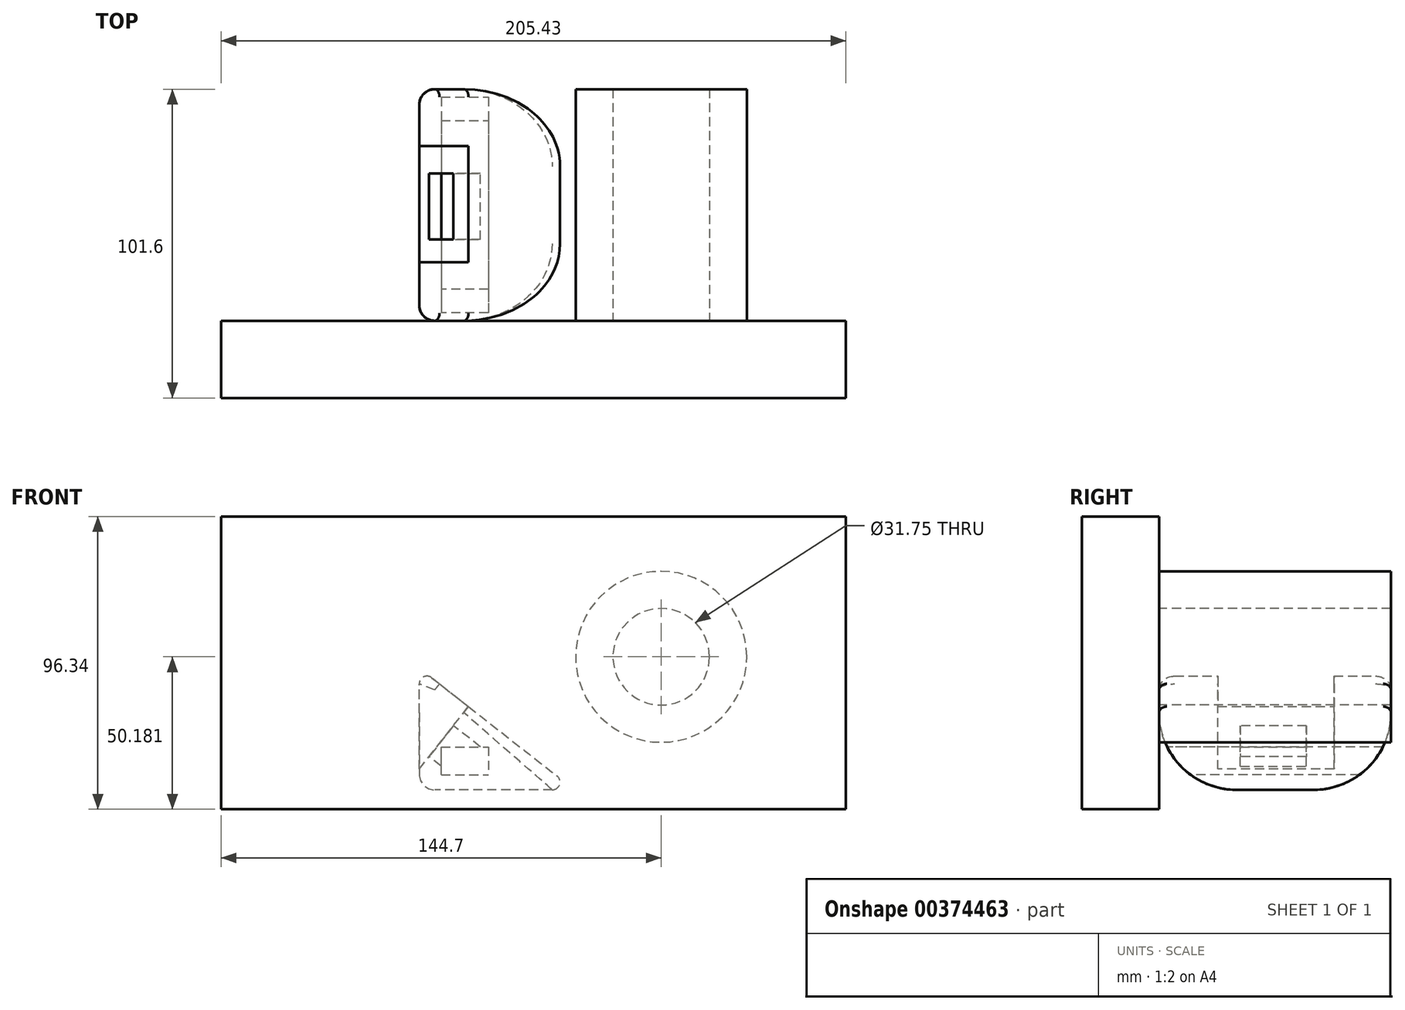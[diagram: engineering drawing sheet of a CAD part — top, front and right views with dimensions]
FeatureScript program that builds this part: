
annotation { "Feature Type Name" : "Feature", "Feature Type Description" : "" }
export const myFeature = defineFeature(function(context is Context, id is Id, definition is map)
    precondition{}
    {
        {
            var Q0;
            Q0=qCreatedBy(makeId("Front.planeOp"),FACE);
            var sketch = newSketch(context, id + "F0", { "sketchPlane" : qUnion([Q0])});
            skLineSegment(sketch, "E0", {"start": v(-51.08, 40.1) * mm, "end": v(0, 0) * mm});
            skLineSegment(sketch, "E1", {"start": v(0, 0) * mm, "end": v(-51.08, 0) * mm});
            skLineSegment(sketch, "E2", {"start": v(-51.08, 0) * mm, "end": v(-51.08, 40.1) * mm});
            skSolve(sketch);
        }
        {
            var Q0;
            Q0 = qSketchRegion(id + "F0", true);
            extrude(context, id + "F1", {"entities" : qUnion([Q0]), "depth" : 76.2 * mm});
        }
        {
            var Q0;
            Q0=qCreatedBy(makeId("Front.planeOp"),FACE);
            var sketch = newSketch(context, id + "F2", { "sketchPlane" : qUnion([Q0])});
            skCircle(sketch, "E3", {"center": v(28.44, 43.78) * mm, "radius": 28.13 * mm});
            skSolve(sketch);
        }
        {
            var Q0;
            Q0=makeQuery(id+"F2.imprint","IMPRINT",FACE,{"disambiguationData":[TD([[makeQuery(id+"F2.imprint","IMPRINT",EDGE,{"derivedFrom":sQuery(id+"F2.wireOp",EDGE,"E3")}),1.0]])]});
            extrude(context, id + "F3", {"entities" : qUnion([Q0]), "depth" : 76.2 * mm});
        }
        {
            var Q0;
            Q0=makeQuery(id+"F3.opExtrude","CAP_FACE",FACE,{"disambiguationData":[OSD([sQuery(id+"F2.wireOp",EDGE,"E3")])],"isStart":false});
            var sketch = newSketch(context, id + "F4", { "sketchPlane" : qUnion([Q0])});
            skCircle(sketch, "E4", {"center": v(28.44, 43.78) * mm, "radius": 15.88 * mm});
            skSolve(sketch);
        }
        {
            var Q0;
            Q0 = qSketchRegion(id + "F4", true);
            extrude(context, id + "F5", {"entities" : qUnion([Q0]), "operationType" : NewBodyOperationType.REMOVE, "endBound" : BoundingType.THROUGH_ALL, "oppositeDirection" : true, "depth" : 25.4 * mm});
        }
        {
            var Q0;
            Q0=makeQuery(id+"F1.opExtrude","SWEPT_FACE",FACE,{"disambiguationData":[OSD([sQuery(id+"F0.wireOp",EDGE,"E0")])]});
            var sketch = newSketch(context, id + "F6", { "sketchPlane" : qUnion([Q0])});
            skLineSegment(sketch, "E5", {"start": v(-64.94, -56.93) * mm, "end": v(-44.4, -56.93) * mm});
            skLineSegment(sketch, "E6", {"start": v(-44.4, -56.93) * mm, "end": v(-44.4, -18.7) * mm});
            skLineSegment(sketch, "E7", {"start": v(-44.4, -18.7) * mm, "end": v(-64.94, -18.7) * mm});
            skLineSegment(sketch, "E8", {"start": v(-64.94, -18.7) * mm, "end": v(-64.94, -56.93) * mm});
            skSolve(sketch);
        }
        {
            var Q0;
            Q0 = qSketchRegion(id + "F6", true);
            extrude(context, id + "F7", {"entities" : qUnion([Q0]), "operationType" : NewBodyOperationType.REMOVE, "endBound" : BoundingType.THROUGH_ALL, "oppositeDirection" : true, "depth" : 25.4 * mm});
        }
        {
            var Q0;
            Q0=makeQuery(id+"F1.opExtrude","CAP_FACE",FACE,{"disambiguationData":[OSD([sQuery(id+"F0.wireOp",EDGE,"E0"),sQuery(id+"F0.wireOp",EDGE,"E1"),sQuery(id+"F0.wireOp",EDGE,"E2")])],"isStart":false});
            var sketch = newSketch(context, id + "F8", { "sketchPlane" : qUnion([Q0])});
            skLineSegment(sketch, "E9.bottom", {"start": v(-13, 23.25) * mm, "end": v(-41.9, 23.25) * mm});
            skLineSegment(sketch, "E9.top", {"start": v(-13, 0) * mm, "end": v(-41.9, 0) * mm});
            skLineSegment(sketch, "E9.left", {"start": v(-13, 23.25) * mm, "end": v(-13, 0) * mm});
            skLineSegment(sketch, "E9.right", {"start": v(-41.9, 23.25) * mm, "end": v(-41.9, 0) * mm});
            skLineSegment(sketch, "E10.bottom", {"start": v(-23.45, 20.65) * mm, "end": v(-51.08, 20.65) * mm});
            skLineSegment(sketch, "E10.top", {"start": v(-23.45, 0) * mm, "end": v(-51.08, 0) * mm});
            skLineSegment(sketch, "E10.left", {"start": v(-23.45, 20.65) * mm, "end": v(-23.45, 0) * mm});
            skLineSegment(sketch, "E10.right", {"start": v(-51.08, 20.65) * mm, "end": v(-51.08, 0) * mm});
            skSolve(sketch);
        }
        {
            var Q0;
            Q0=sQuery(id+"F8.wireOp",EDGE,"E10.left");
            var Q1;
            Q1=sQuery(id+"F8.wireOp",EDGE,"E10.bottom");
            var Q2;
            Q2=sQuery(id+"F8.wireOp",EDGE,"E10.right");
            var Q3;
            Q3=sQuery(id+"F8.wireOp",EDGE,"E10.top");
            extrude(context, id + "F9", {"bodyType" : ToolBodyType.SURFACE, "surfaceEntities" : qUnion([Q0, Q1, Q2, Q3]), "depth" : 25.4 * mm});
        }
        {
            var Q0;
            Q0=makeQuery(id+"F9.opExtrude","SWEPT_BODY",BODY,{"disambiguationData":[OSD([sQuery(id+"F8.wireOp",EDGE,"E10.bottom")])]});
            deleteBodies(context, id + "F10", {"entities" : qUnion([Q0])});
        }
        {
            var Q0;
            Q0=makeQuery(id+"F1.opExtrude","CAP_FACE",FACE,{"disambiguationData":[OSD([sQuery(id+"F0.wireOp",EDGE,"E0"),sQuery(id+"F0.wireOp",EDGE,"E1"),sQuery(id+"F0.wireOp",EDGE,"E2")])],"isStart":false});
            var sketch = newSketch(context, id + "F11", { "sketchPlane" : qUnion([Q0])});
            skLineSegment(sketch, "E11.bottom", {"start": v(-51.08, 0) * mm, "end": v(-51.08, 0) * mm});
            skLineSegment(sketch, "E11.top", {"start": v(-51.08, 0) * mm, "end": v(-51.08, 0) * mm});
            skLineSegment(sketch, "E11.left", {"start": v(-51.08, 0) * mm, "end": v(-51.08, 0) * mm});
            skLineSegment(sketch, "E11.right", {"start": v(-51.08, 0) * mm, "end": v(-51.08, 0) * mm});
            skLineSegment(sketch, "E12.bottom", {"start": v(-28.39, 14.15) * mm, "end": v(-43.87, 14.15) * mm});
            skLineSegment(sketch, "E12.top", {"start": v(-28.39, 4.92) * mm, "end": v(-43.87, 4.92) * mm});
            skLineSegment(sketch, "E12.left", {"start": v(-28.39, 14.15) * mm, "end": v(-28.39, 4.92) * mm});
            skLineSegment(sketch, "E12.right", {"start": v(-43.87, 14.15) * mm, "end": v(-43.87, 4.92) * mm});
            skSolve(sketch);
        }
        {
            var Q0;
            Q0 = qSketchRegion(id + "F11", true);
            extrude(context, id + "F12", {"entities" : qUnion([Q0]), "operationType" : NewBodyOperationType.REMOVE, "endBound" : BoundingType.THROUGH_ALL, "oppositeDirection" : true, "depth" : 25.4 * mm});
        }
        {
            var Q0;
            Q0=makeQuery(id+"F1.opExtrude","CAP_EDGE",EDGE,{"disambiguationData":[OSD([sQuery(id+"F0.wireOp",EDGE,"E1")])],"isStart":false});
            fillet(context, id + "F13", {"entities" : qUnion([Q0]), "radius" : 25.4 * mm, "tangentPropagation" : true, "allowEdgeOverflow" : false});
        }
        {
            var Q0;
            Q0=makeQuery(id+"F1.opExtrude","CAP_EDGE",EDGE,{"disambiguationData":[OSD([sQuery(id+"F0.wireOp",EDGE,"E1")])],"isStart":true});
            fillet(context, id + "F14", {"entities" : qUnion([Q0]), "radius" : 25.4 * mm, "tangentPropagation" : true, "allowEdgeOverflow" : false});
        }
        {
            var Q0;
            Q0=makeQuery(id+"F13.opFillet","BLEND_EDGE",EDGE,{"blendedFrom":[makeQuery(id+"F1.opExtrude","CAP_EDGE",EDGE,{"disambiguationData":[OSD([sQuery(id+"F0.wireOp",EDGE,"E1")])],"isStart":false}),makeQuery(id+"F1.opExtrude","SWEPT_FACE",FACE,{"disambiguationData":[OSD([sQuery(id+"F0.wireOp",EDGE,"E2")])]})],"blendedInto":[makeQuery(id+"F1.opExtrude","SWEPT_FACE",FACE,{"disambiguationData":[OSD([sQuery(id+"F0.wireOp",EDGE,"E2")])]})]});
            fillet(context, id + "F15", {"entities" : qUnion([Q0]), "radius" : 5.08 * mm, "tangentPropagation" : true, "allowEdgeOverflow" : false});
        }
        {
            var Q0;
            Q0=makeQuery(id+"F14.opFillet","BLEND_EDGE",EDGE,{"blendedFrom":[makeQuery(id+"F1.opExtrude","CAP_EDGE",EDGE,{"disambiguationData":[OSD([sQuery(id+"F0.wireOp",EDGE,"E1")])],"isStart":true}),makeQuery(id+"F1.opExtrude","SWEPT_FACE",FACE,{"disambiguationData":[OSD([sQuery(id+"F0.wireOp",EDGE,"E0")])]})],"blendedInto":[makeQuery(id+"F1.opExtrude","SWEPT_FACE",FACE,{"disambiguationData":[OSD([sQuery(id+"F0.wireOp",EDGE,"E0")])]})]});
            fillet(context, id + "F16", {"entities" : qUnion([Q0]), "radius" : 2.54 * mm, "tangentPropagation" : true, "allowEdgeOverflow" : false});
        }
        {
            var Q0;
            Q0=makeQuery(id+"F7.boolean.opBoolean","COPY",FACE,{"derivedFrom":makeQuery(id+"F7.opExtrude","SWEPT_FACE",FACE,{"disambiguationData":[OSD([sQuery(id+"F6.wireOp",EDGE,"E6")])]})});
            var sketch = newSketch(context, id + "F17", { "sketchPlane" : qUnion([Q0])});
            skLineSegment(sketch, "E13.bottom", {"start": v(27.77, -8) * mm, "end": v(49.5, -8) * mm});
            skLineSegment(sketch, "E13.top", {"start": v(27.77, -20.96) * mm, "end": v(49.5, -20.96) * mm});
            skLineSegment(sketch, "E13.left", {"start": v(27.77, -8) * mm, "end": v(27.77, -20.96) * mm});
            skLineSegment(sketch, "E13.right", {"start": v(49.5, -8) * mm, "end": v(49.5, -20.96) * mm});
            skSolve(sketch);
        }
        {
            var Q0;
            Q0 = qSketchRegion(id + "F17", true);
            extrude(context, id + "F18", {"entities" : qUnion([Q0]), "operationType" : NewBodyOperationType.REMOVE, "endBound" : BoundingType.UP_TO_NEXT, "oppositeDirection" : true, "depth" : 25.4 * mm});
        }
        {
            var Q0;
            Q0=makeQuery(id+"F3.opExtrude","CAP_FACE",FACE,{"disambiguationData":[OSD([sQuery(id+"F2.wireOp",EDGE,"E3")])],"isStart":false});
            var sketch = newSketch(context, id + "F19", { "sketchPlane" : qUnion([Q0])});
            skLineSegment(sketch, "E14.bottom", {"start": v(-116.26, 89.94) * mm, "end": v(89.17, 89.94) * mm});
            skLineSegment(sketch, "E14.top", {"start": v(-116.26, -6.4) * mm, "end": v(89.17, -6.4) * mm});
            skLineSegment(sketch, "E14.left", {"start": v(-116.26, 89.94) * mm, "end": v(-116.26, -6.4) * mm});
            skLineSegment(sketch, "E14.right", {"start": v(89.17, 89.94) * mm, "end": v(89.17, -6.4) * mm});
            skSolve(sketch);
        }
        {
            var Q0;
            Q0 = qSketchRegion(id + "F19", true);
            extrude(context, id + "F20", {"entities" : qUnion([Q0]), "depth" : 25.4 * mm});
        }
    });
